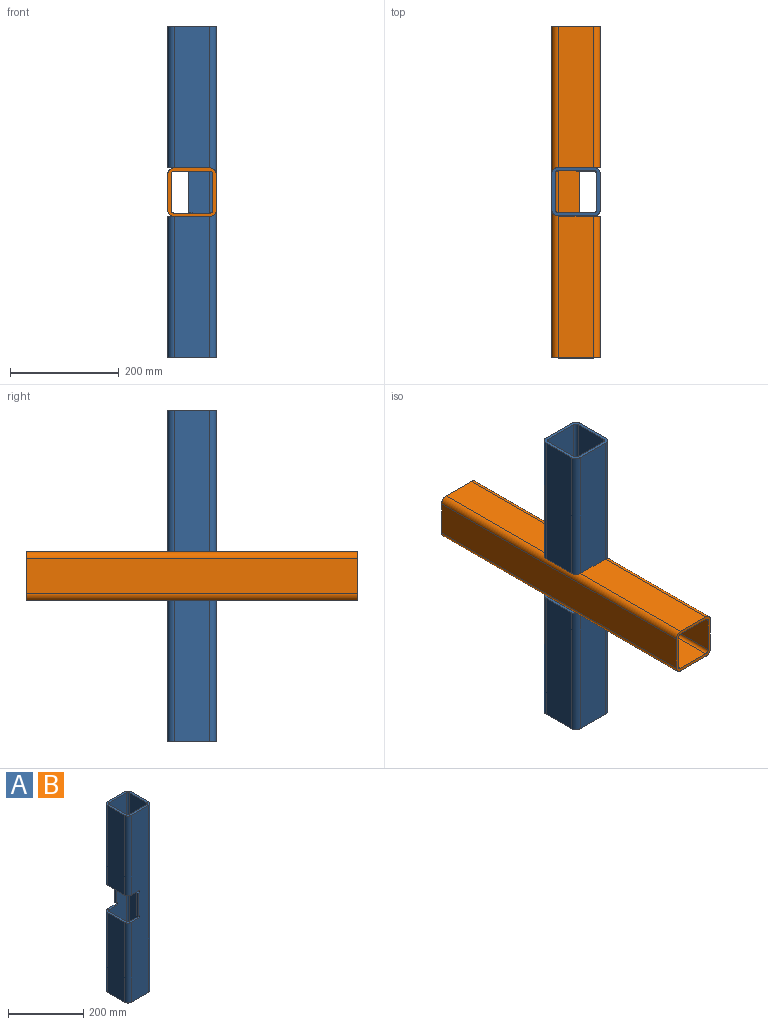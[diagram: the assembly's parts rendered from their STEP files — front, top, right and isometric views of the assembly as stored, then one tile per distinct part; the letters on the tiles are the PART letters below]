
ASSEMBLY  parts=2 mates=1
PART A: 36 faces, bbox 88.9x88.9x609.6 mm
  f0: plane 609.6x65.23mm, normal (0,1,0), area 37347mm2, adj f5,f8,f17,f18,f24,f25,f26,f27
  f1: plane 609.6x65.23mm, normal (0,-1,0), area 37347mm2, adj f4,f10,f20,f21,f24,f25,f26,f27
  f2: plane 609.6x65.23mm, normal (0,-1,0), area 37347mm2, adj f5,f11,f12,f23,f24,f25,f26,f27
  f3: plane 609.6x65.23mm, normal (0,1,0), area 37347mm2, adj f4,f7,f14,f15,f24,f25,f26,f27
  f4: plane 76.2x5.92mm, normal (-1,0,0), area 451mm2, adj f1,f3,f29,f33
  f5: plane 76.2x5.92mm, normal (-1,0,0), area 451mm2, adj f0,f2,f31,f35
  f6: plane 260.35x65.23mm, normal (-1,0,0), area 16981.9mm2, adj f7,f11,f25,f26
  f7: cylinder r=11.84mm len=260.35mm, axis (0,0,-1), area 4840.6mm2, adj f3,f6,f25,f26
  f8: cylinder r=5.92mm len=260.35mm, axis (0,0,-1), area 2420.3mm2, adj f0,f9,f25,f26
  f9: plane 260.35x65.23mm, normal (1,0,0), area 16981.9mm2, adj f8,f10,f25,f26
  f10: cylinder r=5.92mm len=260.35mm, axis (0,0,-1), area 2420.3mm2, adj f1,f9,f25,f26
  f11: cylinder r=11.84mm len=260.35mm, axis (0,0,-1), area 4840.6mm2, adj f2,f6,f25,f26
  f12: cylinder r=11.84mm len=609.6mm, axis (0,0,-1), area 11334mm2, adj f2,f13,f24,f25
  f13: plane 609.6x65.23mm, normal (1,0,0), area 39762.5mm2, adj f12,f14,f24,f25
  f14: cylinder r=11.84mm len=609.6mm, axis (0,0,-1), area 11334mm2, adj f3,f13,f24,f25
  f15: cylinder r=11.84mm len=260.35mm, axis (0,0,-1), area 4840.6mm2, adj f3,f16,f24,f27
  f16: plane 260.35x65.23mm, normal (-1,0,0), area 16981.9mm2, adj f15,f23,f24,f27
  f17: cylinder r=5.92mm len=609.6mm, axis (0,0,-1), area 5667mm2, adj f0,f22,f24,f25
  f18: cylinder r=5.92mm len=260.35mm, axis (0,0,-1), area 2420.3mm2, adj f0,f19,f24,f27
  f19: plane 260.35x65.23mm, normal (1,0,0), area 16981.9mm2, adj f18,f20,f24,f27
  f20: cylinder r=5.92mm len=260.35mm, axis (0,0,-1), area 2420.3mm2, adj f1,f19,f24,f27
  f21: cylinder r=5.92mm len=609.6mm, axis (0,0,-1), area 5667mm2, adj f1,f22,f24,f25
  f22: plane 609.6x65.23mm, normal (-1,0,0), area 39762.5mm2, adj f17,f21,f24,f25
  f23: cylinder r=11.84mm len=260.35mm, axis (0,0,-1), area 4840.6mm2, adj f2,f16,f24,f27
  f24: plane 88.9x88.9mm, normal (0,0,1), area 1874.2mm2, adj f0,f1,f2,f3,f12,f13,f14,f15
  f25: plane 88.9x88.9mm, normal (0,0,-1), area 1874.2mm2, adj f0,f1,f2,f3,f6,f7,f8,f9
  f26: plane 88.9x44.45mm, normal (0,0,1), area 937.1mm2, adj f0,f1,f2,f3,f6,f7,f8,f9
  f27: plane 88.9x44.45mm, normal (0,0,-1), area 937.1mm2, adj f0,f1,f2,f3,f15,f16,f18,f19
  f28: plane 6.35x5.92mm, normal (-1,0,0), area 37.6mm2, adj f1,f3,f26,f29
  f29: plane 6.35x5.92mm, normal (0,0,-1), area 37.6mm2, adj f1,f3,f4,f28
  f30: plane 6.35x5.92mm, normal (-1,0,0), area 37.6mm2, adj f0,f2,f26,f31
  f31: plane 6.35x5.92mm, normal (0,0,-1), area 37.6mm2, adj f0,f2,f5,f30
  f32: plane 6.35x5.92mm, normal (-1,0,0), area 37.6mm2, adj f1,f3,f27,f33
  f33: plane 6.35x5.92mm, normal (0,0,1), area 37.6mm2, adj f1,f3,f4,f32
  f34: plane 6.35x5.92mm, normal (-1,0,0), area 37.6mm2, adj f0,f2,f27,f35
  f35: plane 6.35x5.92mm, normal (0,0,1), area 37.6mm2, adj f0,f2,f5,f34
PART B: same geometry as A
PLACE A t=(48.97,-48.3,14.04)mm
PLACE B rot(axis=(0,-0.71,0.71),180deg) t=(48.97,-48.52,13.83)mm
MATE fastened B.f34 <-> A.f34  axis (1,0,0) through (48.97,-89.79,55.32)mm
